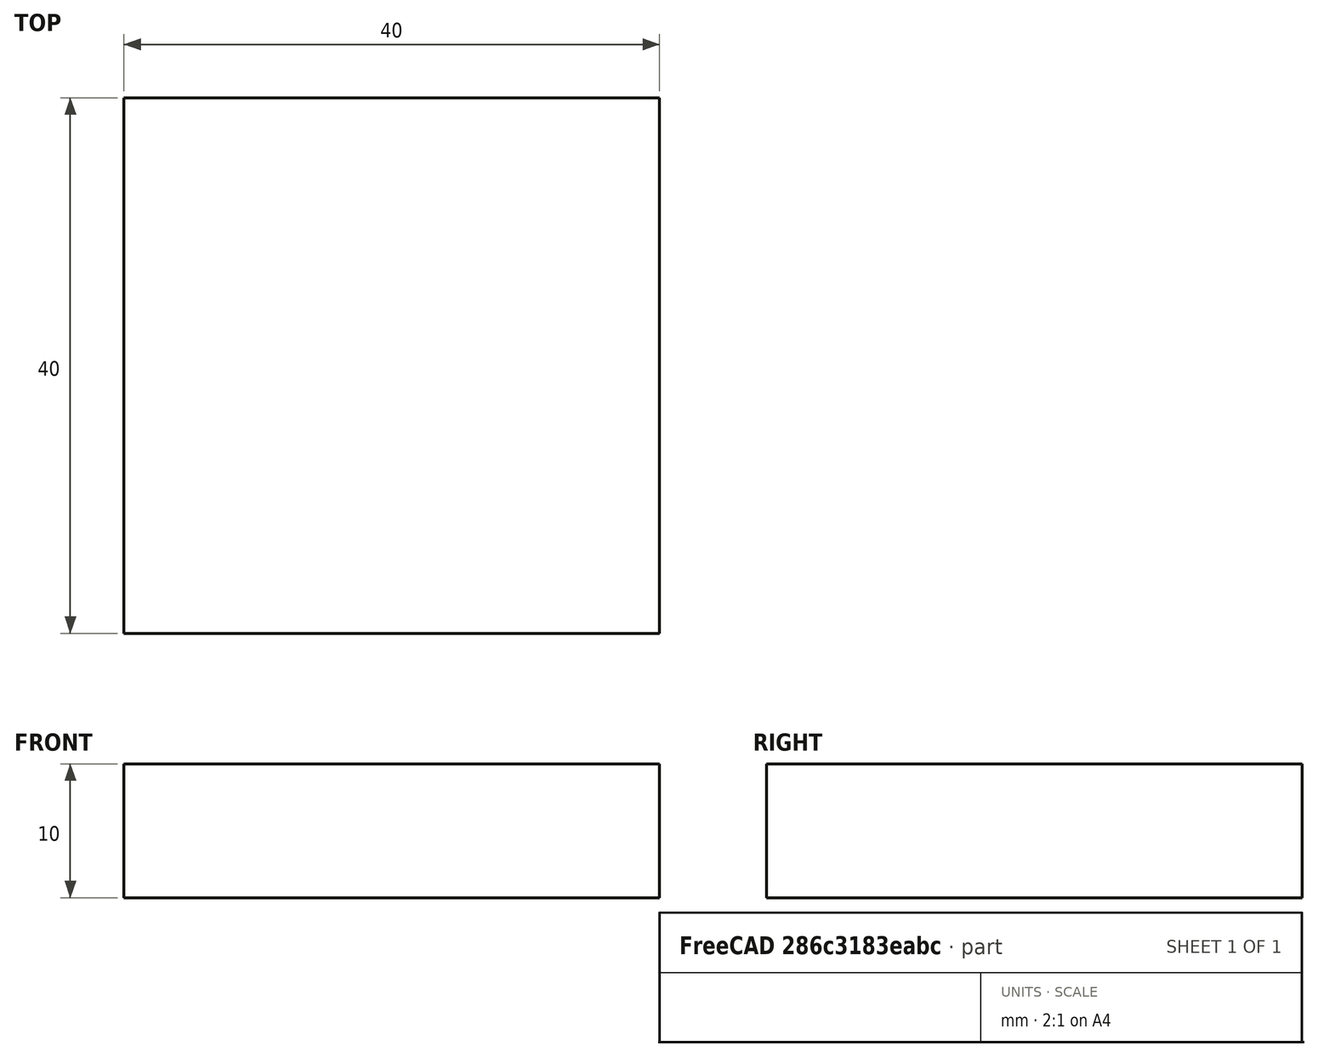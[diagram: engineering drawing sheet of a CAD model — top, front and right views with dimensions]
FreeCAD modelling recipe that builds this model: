
FCSTD DOCUMENT  (FreeCAD 0.19R24366 (Git))
Label: flow_cal_cube_big
License: All rights reserved
LicenseURL: http://en.wikipedia.org/wiki/All_rights_reserved
objects: Sketcher::SketchObject×1, PartDesign::Pad×1, PartDesign::Body×1
note: 4 computed .brp shape members not serialized (recipe doc carries the construction recipe); baked Part::Feature solids carry a one-line shape summary decoded from their .brp

FEATURE [Sketcher::SketchObject] Sketch
  FullyConstrained = true
  MapMode = 5
  Support = -> [XY_Plane]
  sketch-geometry (4):
    g0: LineSegment StartX=-20 StartY=20 StartZ=0 EndX=20 EndY=20 EndZ=0
    g1: LineSegment StartX=20 StartY=20 StartZ=0 EndX=20 EndY=-20 EndZ=0
    g2: LineSegment StartX=20 StartY=-20 StartZ=0 EndX=-20 EndY=-20 EndZ=0
    g3: LineSegment StartX=-20 StartY=-20 StartZ=0 EndX=-20 EndY=20 EndZ=0
  constraints (11):
    c: Coincident(g0,g1)
    c: Coincident(g1,g2)
    c: Coincident(g2,g3)
    c: Coincident(g3,g0)
    c: Horizontal(g0)
    c: Horizontal(g2)
    c: Vertical(g1)
    c: Vertical(g3)
    c: Symmetric(g2,g0,g-1)
    c: Equal(g1,g2)
    c: Distance(g2) = 40
FEATURE [PartDesign::Pad] Pad
  Direction = (1,1,1)
  Length = 10
  Length2 = 100
  Profile = -> Sketch
  Type = 0
FEATURE [PartDesign::Body] Body
  Group = -> [Sketch,Pad]
  Origin = -> Origin
  Tip = -> Pad
